# Revit family: VR6 LED
name_source: partatom
category: Lighting Fixtures
revit_build: Autodesk Revit 2018 (Build: 20181015_0930(x64)
units: mm (PartAtom-declared; Revit-internal decimal feet)

## family parameters
Always vertical = Yes
Cut with Voids When Loaded = No
Light Source = Yes
OmniClass Number = 23.80.70.00
OmniClass Title = Lighting
Part Type = Normal
Room Calculation Point = No
Round Connector Dimension = Use Diameter
Shared = No
Work Plane-Based = No

## types (4) — shared parameters
Color Filter = 16777215
Dimming Lamp Color Temperature Shift = <None>
Emit Shape Visible in Rendering = No
Emit from Rectangle Length = 1000 mm  [stored 3.28084 ft]
Emit from Rectangle Width = 150 mm
Light Source Symbol Size = 300 mm
mount height = 2700 mm  [stored 8.85827 ft]
voltage = 277 V
vr6 guage steel = vr6 guage steel
vr6 screw = vr6 screw
vr6 shade = vr6 shade

## per-type parameters (varying)
| type | Apparent Load |
| VR6 36 LED | 36 VA |
| VR6 40 LED | 40 VA |
| VR6 54 LED | 54 VA |
| VR6 72LED | 72 VA |

note: [stored X ft] marks values corroborated as IEEE doubles in the binary element streams (Revit-internal decimal feet)

## geometry (parser evidence)
native form markers: Sweep x5
no freeform markers — native parametric forms only
